# Revit family: 多级离心泵 - 立式
name_source: partatom
category: 机械设备
units: mm (PartAtom-declared; Revit-internal decimal feet)

## family parameters
共享 = 否
分类 = 泵
加载时剪切的空心 = 否
圆形连接件大小 = 使用半径
基于工作平面 = 否
总是垂直 = 是
房间计算点 = 否
零件类型 = 标准

## types (12) — shared parameters
半径 1 = 20  [stored 0.0656168 ft]
极数 = 3
法兰查找表 = CHS_Flange Flat Face - Integral - Steel - PN 25.csv
泵材质 = <按类别>
泵符号 = 泵符号
电压 = 380 V
负荷分类 = 电气器具 - 居住单元
zero-valued in all types: 默认高程

## per-type parameters (varying)
- 1 CMH - 460.6 m: B1=680; B2=372; D=42.2  [stored 0.138451 ft]; D1=220; D2=188; D3=160; G=320; G1=210; G2=150; H=50  [stored 0.164042 ft]; h=22  [stored 0.0721785 ft]; 公称半径=16 mm; 公称直径=32 mm; 半径 10=19.1; 半径 11=21.1  [stored 0.0692257 ft]; 半径 12=50  [stored 0.164042 ft]; 半径 2=67.5; 半径 3=87.8; 半径 4=40.5  [stored 0.132874 ft]; 半径 5=80; 半径 6=64; 半径 7=110; 半径 8=48  [stored 0.15748 ft]; 半径 9=21.1  [stored 0.0692257 ft]; 法兰半径=70; 法兰厚度=18  [stored 0.0590551 ft]; 法兰直径=140; 视在负荷=8 kW; 重量=65 kg; 长度 1=54.8; 长度 2=20  [stored 0.0656168 ft]; 长度 3=31.2  [stored 0.102362 ft]; 长度 4=128; 长度 5=84; 长度 6=86.6; 长度 7=25  [stored 0.082021 ft]; 高度 1=124; 高度 2=53.1; 高度 3=93; 高度 4=62.4
- 3 CMH - 460.6 m: B1=680; B2=372; D=42.2  [stored 0.138451 ft]; D1=220; D2=188; D3=160; G=320; G1=210; G2=150; H=50  [stored 0.164042 ft]; h=22  [stored 0.0721785 ft]; 公称半径=16 mm; 公称直径=32 mm; 半径 10=19.1; 半径 11=21.1  [stored 0.0692257 ft]; 半径 12=50  [stored 0.164042 ft]; 半径 2=67.5; 半径 3=87.8; 半径 4=40.5  [stored 0.132874 ft]; 半径 5=80; 半径 6=64; 半径 7=110; 半径 8=48  [stored 0.15748 ft]; 半径 9=21.1  [stored 0.0692257 ft]; 法兰半径=70; 法兰厚度=18  [stored 0.0590551 ft]; 法兰直径=140; 视在负荷=8 kW; 重量=99 kg; 长度 1=54.8; 长度 2=20  [stored 0.0656168 ft]; 长度 3=31.2  [stored 0.102362 ft]; 长度 4=128; 长度 5=84; 长度 6=86.6; 长度 7=25  [stored 0.082021 ft]; 高度 1=124; 高度 2=53.1; 高度 3=93; 高度 4=62.4
- 5 CMH - 450.8 m: B1=311; B2=191; D=42.2  [stored 0.138451 ft]; D1=141; D2=109; D3=0  [stored 0 ft]; G=320; G1=210; G2=150; H=50  [stored 0.164042 ft]; h=22  [stored 0.0721785 ft]; 公称半径=16 mm; 公称直径=32 mm; 半径 10=19.1; 半径 11=21.1  [stored 0.0692257 ft]; 半径 12=50  [stored 0.164042 ft]; 半径 2=67.5; 半径 3=87.8; 半径 4=40.5  [stored 0.132874 ft]; 半径 5=60.8; 半径 6=48.6; 半径 7=70.5; 半径 8=36.5; 半径 9=21.1  [stored 0.0692257 ft]; 法兰半径=70; 法兰厚度=18  [stored 0.0590551 ft]; 法兰直径=140; 视在负荷=6 kW; 重量=18 kg; 长度 1=54.8; 长度 2=20  [stored 0.0656168 ft]; 长度 3=15.4; 长度 4=128; 长度 5=84; 长度 6=86.6; 长度 7=25  [stored 0.082021 ft]; 高度 1=63.7; 高度 2=27.3; 高度 3=47.8; 高度 4=30.8
- 10 CMH - 431.2 m: B1=357; B2=231; D=60.1  [stored 0.197178 ft]; D1=141; D2=109; D3=0  [stored 0 ft]; G=248; G1=261; G2=200; H=80; h=26  [stored 0.0853018 ft]; 公称半径=25 mm; 公称直径=50 mm; 半径 10=28.1; 半径 11=30.1; 半径 12=80; 半径 2=90; 半径 3=117; 半径 4=54  [stored 0.177165 ft]; 半径 5=81; 半径 6=64.8; 半径 7=70.5; 半径 8=48.6; 半径 9=30.1; 法兰半径=82.5; 法兰厚度=20  [stored 0.0656168 ft]; 法兰直径=165; 视在负荷=8 kW; 重量=31 kg; 长度 1=70.7; 长度 2=20  [stored 0.0656168 ft]; 长度 3=15.4; 长度 4=99.2; 长度 5=104.4; 长度 6=138.6; 长度 7=40  [stored 0.131234 ft]; 高度 1=77; 高度 2=33  [stored 0.108268 ft]; 高度 3=57.8; 高度 4=30.8
- 15 CMH - 450.8 m: B1=463; B2=335; D=60.1  [stored 0.197178 ft]; D1=198; D2=120; D3=0  [stored 0 ft]; G=248; G1=261; G2=200; H=90; h=26  [stored 0.0853018 ft]; 公称半径=25 mm; 公称直径=50 mm; 半径 10=28.1; 半径 11=30.1; 半径 12=90; 半径 2=90; 半径 3=117; 半径 4=54  [stored 0.177165 ft]; 半径 5=81; 半径 6=64.8; 半径 7=99; 半径 8=48.6; 半径 9=30.1; 法兰半径=82.5; 法兰厚度=20  [stored 0.0656168 ft]; 法兰直径=165; 视在负荷=15 kW; 重量=48 kg; 长度 1=70.7; 长度 2=20  [stored 0.0656168 ft]; 长度 3=8.4; 长度 4=99.2; 长度 5=104.4; 长度 6=155.9; 长度 7=45  [stored 0.147638 ft]; 高度 1=111.7; 高度 2=47.9; 高度 3=83.8; 高度 4=16.8
- 20 CMH - 470.4 m: B1=463; B2=372; D=60.1  [stored 0.197178 ft]; D1=220; D2=134; D3=0  [stored 0 ft]; G=248; G1=261; G2=200; H=90; h=26  [stored 0.0853018 ft]; 公称半径=25 mm; 公称直径=50 mm; 半径 10=28.1; 半径 11=30.1; 半径 12=90; 半径 2=90; 半径 3=117; 半径 4=54  [stored 0.177165 ft]; 半径 5=81; 半径 6=64.8; 半径 7=110; 半径 8=48.6; 半径 9=30.1; 法兰半径=82.5; 法兰厚度=20  [stored 0.0656168 ft]; 法兰直径=165; 视在负荷=19 kW; 重量=59 kg; 长度 1=70.7; 长度 2=20  [stored 0.0656168 ft]; 长度 3=9.6; 长度 4=99.2; 长度 5=104.4; 长度 6=155.9; 长度 7=45  [stored 0.147638 ft]; 高度 1=124; 高度 2=53.1; 高度 3=93; 高度 4=19.2
- 32 CMH - 382.2 m: B1=895; B2=499; D=185; D1=260; D2=172; D3=350; G=298; G1=320; G2=226; H=105; h=30  [stored 0.0984252 ft]; 公称半径=33 mm; 公称直径=65 mm; 半径 10=64.8; 半径 11=92.5; 半径 12=105; 半径 2=101.7; 半径 3=132.2; 半径 4=61; 半径 5=175; 半径 6=140; 半径 7=130; 半径 8=105; 半径 9=92.5; 法兰半径=92.5; 法兰厚度=22  [stored 0.0721785 ft]; 法兰直径=185; 视在负荷=19 kW; 重量=139 kg; 长度 1=79; 长度 2=22  [stored 0.0721785 ft]; 长度 3=16.8; 长度 4=119.2; 长度 5=128; 长度 6=181.9; 长度 7=52.5; 高度 1=166.3; 高度 2=71.3; 高度 3=124.8; 高度 4=33.6
- 45 CMH - 382.2 m: B1=829; B2=499; D=200; D1=260; D2=172; D3=350; G=331; G1=365; G2=248; H=140; h=45  [stored 0.147638 ft]; 公称半径=40 mm; 公称直径=80 mm; 半径 10=70; 半径 11=100; 半径 12=140; 半径 2=111.6; 半径 3=145.1; 半径 4=67; 半径 5=175; 半径 6=140; 半径 7=130; 半径 8=105; 半径 9=100; 法兰半径=100; 法兰厚度=24  [stored 0.0787402 ft]; 法兰直径=200; 视在负荷=30 kW; 重量=144 kg; 长度 1=86; 长度 2=24  [stored 0.0787402 ft]; 长度 3=16.8; 长度 4=132.4; 长度 5=146; 长度 6=242.5; 长度 7=70; 高度 1=166.3; 高度 2=71.3; 高度 3=124.8; 高度 4=33.6
- 64 CMH - 382.2 m: B1=754; B2=499; D=235; D1=260; D2=172; D3=350; G=331; G1=365; G2=248; H=140; h=45  [stored 0.147638 ft]; 公称半径=50 mm; 公称直径=100 mm; 半径 10=82.3; 半径 11=117.5; 半径 12=140; 半径 2=111.6; 半径 3=145.1; 半径 4=67; 半径 5=175; 半径 6=140; 半径 7=130; 半径 8=105; 半径 9=117.5; 法兰半径=117.5; 法兰厚度=24  [stored 0.0787402 ft]; 法兰直径=235; 视在负荷=45 kW; 重量=143 kg; 长度 1=86; 长度 2=24  [stored 0.0787402 ft]; 长度 3=16.8; 长度 4=132.4; 长度 5=146; 长度 6=242.5; 长度 7=70; 高度 1=166.3; 高度 2=71.3; 高度 3=124.8; 高度 4=33.6
- 90 CMH - 392.0 m: B1=571; B2=391; D=235; D1=220; D2=134; D3=300; G=348; G1=380; G2=261; H=140; h=45  [stored 0.147638 ft]; 公称半径=50 mm; 公称直径=100 mm; 半径 10=82.3; 半径 11=117.5; 半径 12=140; 半径 2=117.5; 半径 3=152.7; 半径 4=70.5; 半径 5=150; 半径 6=120; 半径 7=110; 半径 8=90; 半径 9=117.5; 法兰半径=117.5; 法兰厚度=24  [stored 0.0787402 ft]; 法兰直径=235; 视在负荷=45 kW; 重量=109 kg; 长度 1=90.1; 长度 2=24  [stored 0.0787402 ft]; 长度 3=9.6; 长度 4=139.2; 长度 5=152; 长度 6=242.5; 长度 7=70; 高度 1=130.3; 高度 2=55.9; 高度 3=97.8; 高度 4=19.2
- 120 CMH - 392.0 m: B1=834; B2=499; D=235; D1=260; D2=172; D3=350; G=348; G1=380; G2=261; H=140; h=45  [stored 0.147638 ft]; 公称半径=50 mm; 公称直径=100 mm; 半径 10=82.3; 半径 11=117.5; 半径 12=140; 半径 2=117.5; 半径 3=152.7; 半径 4=70.5; 半径 5=175; 半径 6=140; 半径 7=130; 半径 8=105; 半径 9=117.5; 法兰半径=117.5; 法兰厚度=24  [stored 0.0787402 ft]; 法兰直径=235; 视在负荷=75 kW; 重量=175 kg; 长度 1=90.1; 长度 2=24  [stored 0.0787402 ft]; 长度 3=16.8; 长度 4=139.2; 长度 5=152; 长度 6=242.5; 长度 7=70; 高度 1=166.3; 高度 2=71.3; 高度 3=124.8; 高度 4=33.6
- 150 CMH - 382.2 m: B1=834; B2=499; D=270; D1=260; D2=172; D3=350; G=472; G1=380; G2=344; H=180; h=43  [stored 0.141076 ft]; 公称半径=63 mm; 公称直径=125 mm; 半径 10=94.5; 半径 11=135; 半径 12=180; 半径 2=154.8; 半径 3=201.2; 半径 4=92.9; 半径 5=175; 半径 6=140; 半径 7=130; 半径 8=105; 半径 9=135; 法兰半径=135; 法兰厚度=26  [stored 0.0853018 ft]; 法兰直径=270; 视在负荷=75 kW; 重量=172 kg; 长度 1=116.5; 长度 2=26  [stored 0.0853018 ft]; 长度 3=16.8; 长度 4=188.8; 长度 5=152; 长度 6=311.8; 长度 7=90; 高度 1=166.3; 高度 2=71.3; 高度 3=124.8; 高度 4=33.6

note: [stored X ft] marks values corroborated as IEEE doubles in the binary element streams (Revit-internal decimal feet)

## geometry (parser evidence)
native form markers: Blend x1
no freeform markers — native parametric forms only
